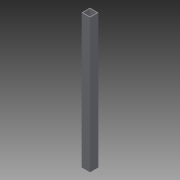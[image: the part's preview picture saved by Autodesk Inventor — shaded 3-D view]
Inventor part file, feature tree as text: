
AUTODESK INVENTOR PART (.ipt)
format: ipt  version: 2013 (Build 170138000, 138)  size: 79,872 bytes
history: native  units: in
note: dims shown in document units (in); Inventor stores cm internally (conversion verified against a paired STEP export)
features: other x2, extrude x1, sketch x1
ambient origin geometry x8: Origin, YZ Plane, XZ Plane, XY Plane, X Axis, Y Axis, Z Axis, Center Point
bodies: Solid1 (feature_tree)
feature tree (4):
  other  "Table"
  other  "Part15-01"
  extrude  "Extrusion1"  Depth=1.5in
  sketch  "Sketch1"  dims[d0=1.5in d1=1.5in d2=0.125in d4=0.0in]
